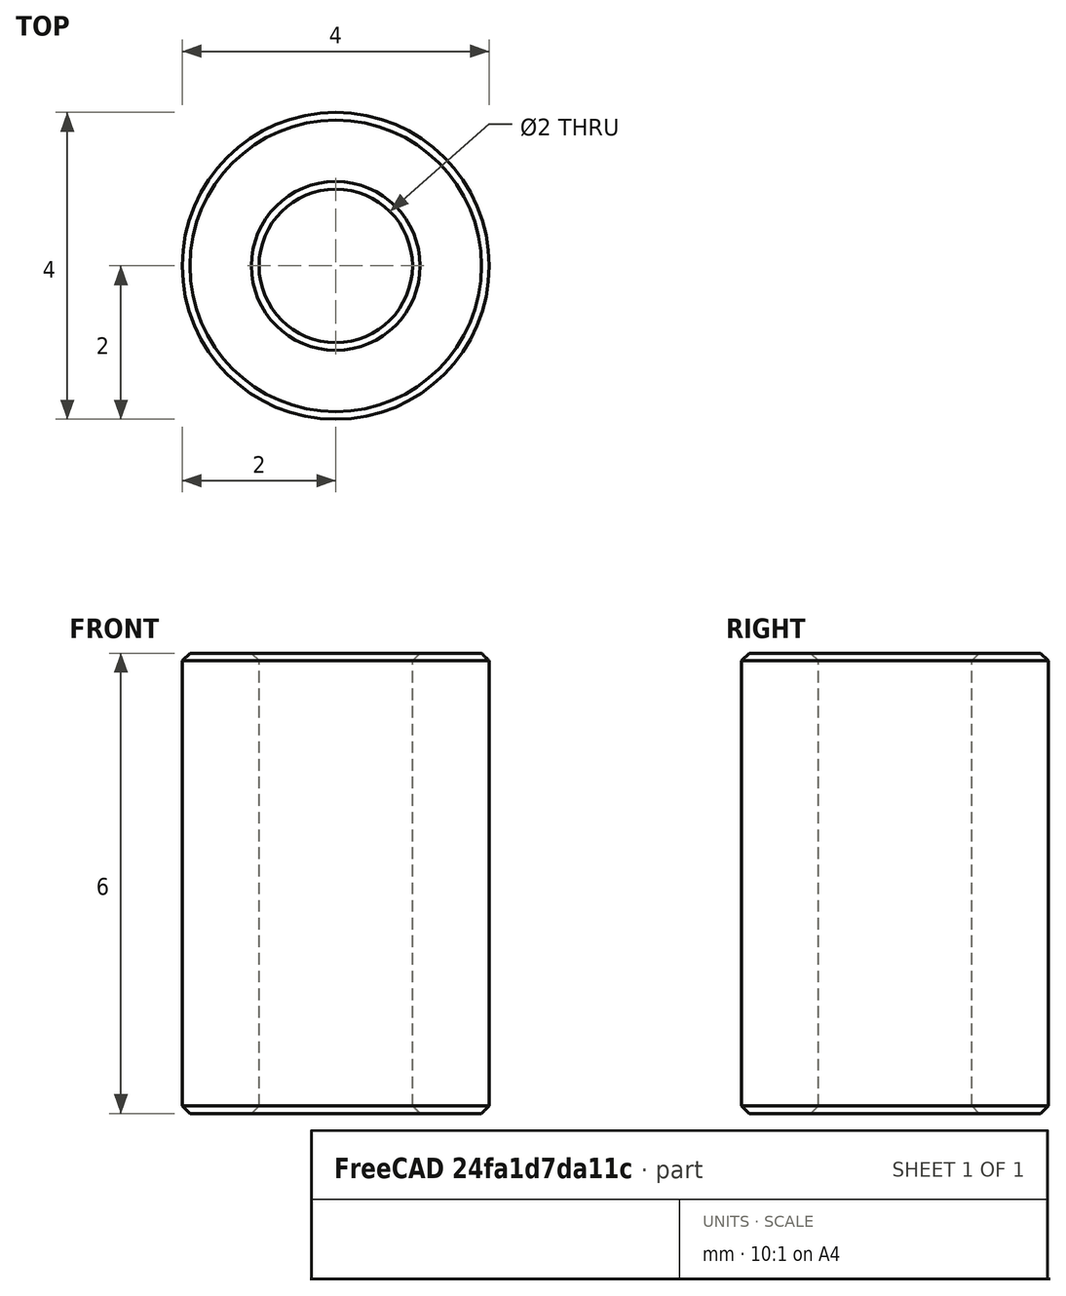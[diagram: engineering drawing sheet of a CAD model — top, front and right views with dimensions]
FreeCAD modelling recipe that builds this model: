
FCSTD DOCUMENT  (FreeCAD 0.14R3702 (Git))
Label: hotend-short-metal-tube
License: CC-BY 3.0
LicenseURL: http://creativecommons.org/licenses/by/3.0/
objects: Part::Feature×2, Sketcher::SketchObject×1, PartDesign::Revolution×1
note: 5 computed .brp shape members not serialized (recipe doc carries the construction recipe); baked Part::Feature solids carry a one-line shape summary decoded from their .brp

FEATURE [Part::Feature] Part__Feature  label="Extruder_short-metal-tube"
  shape: bbox 4 x 4 x 6 mm, 8 faces (baked)
FEATURE [Sketcher::SketchObject] Sketch  label="main-body-sketch"
  Placement = pos=(0,0,0) rot=(-1,0,0;4.71239rad)
  sketch-geometry (10):
    g0: LineSegment StartX=-1.1 StartY=0 StartZ=0 EndX=-1.9 EndY=0 EndZ=0
    g1: LineSegment StartX=-1.9 StartY=0 StartZ=0 EndX=-2 EndY=0.1 EndZ=0
    g2: LineSegment StartX=-2 StartY=0.1 StartZ=0 EndX=-2 EndY=5.9 EndZ=0
    g3: LineSegment StartX=-2 StartY=5.9 StartZ=0 EndX=-1.9 EndY=6 EndZ=0
    g4: LineSegment StartX=-1.9 StartY=6 StartZ=0 EndX=-1.1 EndY=6 EndZ=0
    g5: LineSegment StartX=-1.1 StartY=6 StartZ=0 EndX=-1 EndY=5.9 EndZ=0
    g6: LineSegment StartX=-1 StartY=5.9 StartZ=0 EndX=-1 EndY=0.1 EndZ=0
    g7: LineSegment StartX=-1 StartY=0.1 StartZ=0 EndX=-1.1 EndY=0 EndZ=0
    g8: LineSegment [constr] StartX=-2 StartY=5.9 StartZ=0 EndX=-1 EndY=5.9 EndZ=0
    g9: LineSegment [constr] StartX=-2 StartY=0.1 StartZ=0 EndX=-1 EndY=0.1 EndZ=0
  constraints (28):
    c: PointOnObject(g0,g-1)
    c: Horizontal(g0)
    c: Coincident(g0,g1)
    c: Coincident(g1,g2)
    c: Vertical(g2)
    c: Coincident(g2,g3)
    c: Coincident(g3,g4)
    c: Horizontal(g4)
    c: Coincident(g4,g5)
    c: Coincident(g5,g6)
    c: Vertical(g6)
    c: Coincident(g6,g7)
    c: Coincident(g7,g0)
    c: DistanceX(g-1,g5) = -1
    c: DistanceX(g-1,g2) = -2
    c: DistanceY(g0,g3) = 6
    c: Horizontal(g8)
    c: Coincident(g8,g2)
    c: Coincident(g8,g5)
    c: Angle(g8,g3) = 0.785398
    c: Angle(g5,g8) = 0.785398
    c: DistanceX(g2,g3) = 0.1
    c: Horizontal(g9)
    c: Coincident(g9,g1)
    c: Coincident(g9,g6)
    c: Angle(g1,g9) = 0.785398
    c: Angle(g9,g7) = 0.785398
    c: DistanceX(g0,g1) = -0.1
FEATURE [PartDesign::Revolution] Revolution  label="main-body"
  Angle = 360
  Axis = (0,0,1)
  Base = (0,0,0)
  Placement = pos=(0,0,0) rot=(-1,0,0;4.71239rad)
  ReferenceAxis = -> Sketch [V_Axis]
  Sketch = -> Sketch
FEATURE [Part::Feature] Revolution001  label="hotend-short-metal-tube-final"
  Placement = pos=(0,0,0) rot=(1,0,0;1.5708rad)
  shape: bbox 4 x 4 x 6 mm, 8 faces (baked)
